# Revit family: PF_GEN_Qmax Neo_300_ACO
name_source: partatom
category: Plumbing Fixtures
units: mm (PartAtom-declared; Revit-internal decimal feet)

## family parameters
Always vertical = No
Cut with Voids When Loaded = Yes
OmniClass Number = 23.70.50.24
OmniClass Title = Rainwater Removal
Part Type = Normal
Room Calculation Point = No
Round Connector Dimension = Use Diameter
Shared = No
Work Plane-Based = Yes

## types (1)
- Qmax Neo - 300
    Default Elevation = 0 mm  [stored 0 ft]
    Description = QMAX Neo 300 Guss Qflow 1m anti floating
    Fax = --
    IfcDescription = QMAX Neo 300 Guss Qflow 1m anti floating
    IfcExportAs = IfcWasteTerminalType
    IfcExportType = USERDEFINED
    Manufacturer = ACO
    Model = ACO QMAX Neo 300 Guss Qflow
    RSen_C_code_manufacturer_gln = --
    RSen_C_code_specification_URL = https://www.aco.de
    RSen_C_content_date_changed = 17-09-2024
    RSen_C_content_version = 1.0
    RSen_C_depth = 561 mm
    RSen_C_info_commercial = https://www.aco.de
    RSen_C_info_technical = https://www.aco.de
    RSen_C_intended_use = Drainage systems
    RSen_C_length = 1000 mm  [stored 3.28084 ft]
    RSen_C_material = PE, Black
    RSen_C_material_01 = Iron, Ductile
    RSen_C_width = 366 mm
    Telephone = --
    Type Comments = --
    URL = https://www.aco.de
    installation_manual = https://www.aco.de
    instructions_for_use = https://www.aco.de
    region_index = 1
    slot_width = 25 mm  [stored 0.082021 ft]

note: [stored X ft] marks values corroborated as IEEE doubles in the binary element streams (Revit-internal decimal feet)

## geometry (parser evidence)
native form markers: Sweep x2
no freeform markers — native parametric forms only
